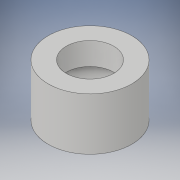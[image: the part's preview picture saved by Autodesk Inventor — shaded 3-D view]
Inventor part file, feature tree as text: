
AUTODESK INVENTOR PART (.ipt)
format: ipt  version: 2019 (Build 230136000, 136)  size: 108,544 bytes
history: native  units: mm
features: extrude x2, sketch x2
ambient origin geometry x8: Origin, YZ Plane, XZ Plane, XY Plane, X Axis, Y Axis, Z Axis, Center Point
bodies: Solid1 (feature_tree)
feature tree (4):
  extrude  "Extrusion1"  Depth=11.5mm
  extrude  "Extrusion2"  Depth=3.1mm
  sketch  "Sketch1"  dims[d0=9.17mm d1=11.5mm]
  sketch  "Sketch2"  dims[d2=4.1mm d3=0.0mm d4=6.52mm d5=3.1mm d6=0.0mm d7=11.5mm]
